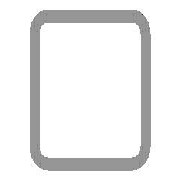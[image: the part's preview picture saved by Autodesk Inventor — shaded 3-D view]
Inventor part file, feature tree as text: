
AUTODESK INVENTOR PART (.ipt)
format: ipt  version: 2024.3 (Build 283343000, 343)  size: 156,672 bytes
history: native  units: mm (DEFAULTED — no unit token found)
features: other x4, sketch x2, extrude x1, plane x1
ambient origin geometry x8: Origin, YZ Plane, XZ Plane, XY Plane, X Axis, Y Axis, Z Axis, Center Point
bodies: Solid1 (feature_tree), Body (feature_tree)
feature tree (8):
  parser-record x1  (decoder bookkeeping rows leaked as tree rows — omitted from the tree; the rows remain in map.json)
  other  "Driven Length"
  other  "Start Plane"
  other  "End Plane"
  extrude  "Extrusion2"  TaperAngle=0.0deg  [1 undecoded]
  sketch  "Sketch3"  dims[d3=94.752309mm d4=0.0mm]
  plane  "Work Plane3"
  sketch  "Sketch5"  dims[d7=4.0mm d9=20.0mm d11=20.0mm d12=2.0mm d13=-0.0mm d14=94.752309mm d15=10.0mm d16=10.0mm d17=90.0deg d18=94.752309mm d19=45.0deg d22=0.0mm d23=0.0mm]
note: 1 required parameter value undecoded (feature->parameter linkage not recoverable at this tier; creation-order binding heuristic only, values carry confidence <= 0.55)
